# Revit family: Sanitary_Showers_AXOR_49626CHN-AXOR-Citterio-C-Porter-unit-120_new
name_source: partatom
category: Plumbing Fixtures
units: mm (PartAtom-declared; Revit-internal decimal feet)

## family parameters
Always vertical = No
Cut with Voids When Loaded = No
OmniClass Number = 23.31.17.00
OmniClass Title = Showers
Part Type = Normal
Room Calculation Point = No
Round Connector Dimension = Use Diameter
Shared = No
Work Plane-Based = Yes

## types (1)
- Default - please load Revit Family Type Catalog
    Connector Description = Water Inlet 12.7mm
    Default Elevation = 1219 mm
    Description = AXOR Citterio C Porter unit 120/120 softsquare with baton hand shower 2jet and textile shower hose
    Diameter = 13 mm
    Manufacturer = AXOR
    Material = AXOR - Metal - 007 Chrome
    Model = 49626CHN
    Product Guid = 99ec3341-2bab-48f3-806f-f488b8dfbb2f
    Product Page URL = https://www.axor-design.com
    Product data url = https://bimobject.com
    URL = https://www.axor-design.com
    Version = 1

## geometry (parser evidence)
native form markers: Sweep x2
no freeform markers — native parametric forms only
